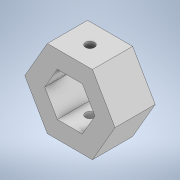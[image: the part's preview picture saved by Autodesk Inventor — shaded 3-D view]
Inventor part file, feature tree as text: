
AUTODESK INVENTOR PART (.ipt)
format: ipt  version: 2022 (Build 260153000, 153)  size: 124,416 bytes
history: native  units: mm
features: extrude x2, sketch x2
ambient origin geometry x8: Origin, YZ Plane, XZ Plane, XY Plane, X Axis, Y Axis, Z Axis, Center Point
bodies: Body1 (feature_tree)
feature tree (4):
  extrude  "Extrusion4"  Depth=60.0mm TaperAngle=360.0deg
  extrude  "Extrusion5"  Depth=2.5mm
  sketch  "Sketch5"  dims[d9=3.1mm d10=60.0mm d12=360.0deg]
  sketch  "Sketch6"  dims[d14=0.45mm d15=2.5mm d16=5.8mm d17=0.0mm d18=1.3mm d19=15.0mm d20=0.0mm]
